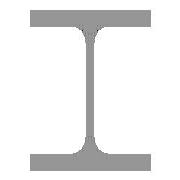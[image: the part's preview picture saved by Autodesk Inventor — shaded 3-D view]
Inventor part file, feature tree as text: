
AUTODESK INVENTOR PART (.ipt)
format: ipt  version: 2025 (Build 290162010, 162A)  size: 143,360 bytes
history: native  units: mm (DEFAULTED — no unit token found)
features: other x3, sketch x2, plane x1
ambient origin geometry x8: Origin, YZ Plane, XZ Plane, XY Plane, X Axis, Y Axis, Z Axis, Center Point
bodies: Solid1 (feature_tree), Body (feature_tree)
feature tree (6):
  other  "Driven Length"
  other  "Start plane"
  other  "End plane"
  sketch  "Sketch2"  dims[d0=8.0mm]
  sketch  "Sketch3"  dims[d1=140.0mm d2=2.0mm d3=12.0mm d4=1.0mm d5=7.0mm d6=8.0mm d7=140.0mm d8=3000.0mm d9=0.0mm d13=12.0mm d14=70.0mm d15=70.0mm d16=-0.0mm d17=3000.0mm d18=90.0deg d19=3000.0mm]
  plane  "Work Plane3"
